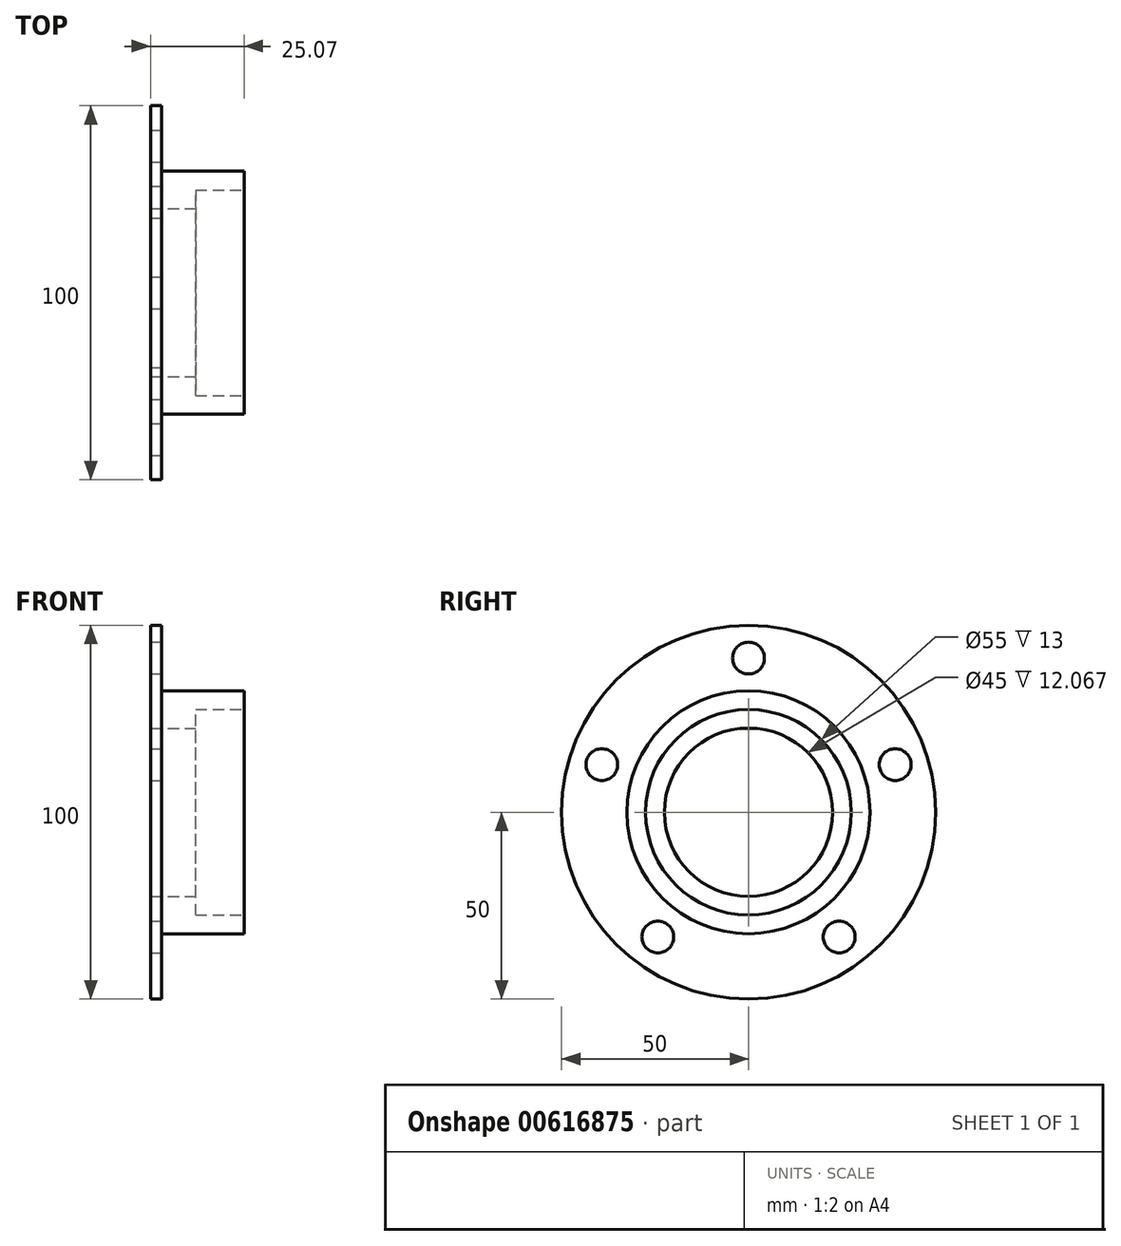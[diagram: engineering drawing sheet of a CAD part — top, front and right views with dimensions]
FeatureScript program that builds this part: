
annotation { "Feature Type Name" : "Feature", "Feature Type Description" : "" }
export const myFeature = defineFeature(function(context is Context, id is Id, definition is map)
    precondition{}
    {
        {
            var Q0;
            Q0=qCreatedBy(makeId("Front.planeOp"),FACE);
            var sketch = newSketch(context, id + "F0", { "sketchPlane" : qUnion([Q0])});
            skLineSegment(sketch, "E0", {"start": v(-2.43, 27.5) * mm, "end": v(-15.43, 27.5) * mm});
            skLineSegment(sketch, "E1", {"start": v(-15.43, 27.5) * mm, "end": v(-15.43, 22.5) * mm});
            skLineSegment(sketch, "E2", {"start": v(-15.43, 22.5) * mm, "end": v(-27.5, 22.5) * mm});
            skLineSegment(sketch, "E3", {"start": v(0, 0) * mm, "end": v(-125.94, 0) * mm, "construction": true});
            skLineSegment(sketch, "E4", {"start": v(-27.5, 22.5) * mm, "end": v(-27.5, 50) * mm});
            skLineSegment(sketch, "E5", {"start": v(-27.5, 50) * mm, "end": v(-24.5, 50) * mm});
            skLineSegment(sketch, "E6", {"start": v(-24.5, 50) * mm, "end": v(-24.5, 32.5) * mm});
            skLineSegment(sketch, "E7", {"start": v(-24.5, 32.5) * mm, "end": v(-2.43, 32.5) * mm});
            skLineSegment(sketch, "E8", {"start": v(-2.43, 32.5) * mm, "end": v(-2.43, 27.5) * mm});
            skSolve(sketch);
        }
        {
            var Q0;
            Q0=makeQuery(id+"F0.imprint","IMPRINT",FACE,{"disambiguationData":[TD([[makeQuery(id+"F0.imprint","IMPRINT",EDGE,{"derivedFrom":sQuery(id+"F0.wireOp",EDGE,"E0")}),-1.0]])]});
            var Q1;
            Q1=sQuery(id+"F0.wireOp",EDGE,"E3");
            revolve(context, id + "F1", {"surfaceOperationType" : NewSurfaceOperationType.NEW, "entities" : qUnion([Q0]), "axis" : qUnion([Q1]), "revolveType" : RevolveType.FULL});
        }
        {
            var Q0;
            Q0=makeQuery(id+"F1.opRevolve","SWEPT_FACE",FACE,{"disambiguationData":[OSD([sQuery(id+"F0.wireOp",EDGE,"E4")])]});
            var sketch = newSketch(context, id + "F2", { "sketchPlane" : qUnion([Q0])});
            skCircle(sketch, "E9", {"center": v(0, 0) * mm, "radius": 41.25 * mm, "construction": true});
            skCircle(sketch, "E10", {"center": v(0, 41.25) * mm, "radius": 5 * mm, "construction": true});
            skCircle(sketch, "E11.1.0", {"center": v(-39.23, 12.75) * mm, "radius": 5 * mm, "construction": true});
            skCircle(sketch, "E11.2.0", {"center": v(-24.25, -33.37) * mm, "radius": 5 * mm, "construction": true});
            skCircle(sketch, "E11.3.0", {"center": v(24.25, -33.37) * mm, "radius": 5 * mm, "construction": true});
            skCircle(sketch, "E11.4.0", {"center": v(39.23, 12.75) * mm, "radius": 5 * mm, "construction": true});
            skSolve(sketch);
        }
        {
            var Q0;
            Q0=sQuery(id+"F2.wireOp",VERTEX,"E10.center");
            var Q1;
            Q1=sQuery(id+"F2.wireOp",VERTEX,"E11.7.0.center");
            var Q2;
            Q2=sQuery(id+"F2.wireOp",VERTEX,"E11.6.0.center");
            var Q3;
            Q3=sQuery(id+"F2.wireOp",VERTEX,"E11.5.0.center");
            var Q4;
            Q4=sQuery(id+"F2.wireOp",VERTEX,"E11.4.0.center");
            var Q5;
            Q5=sQuery(id+"F2.wireOp",VERTEX,"E11.3.0.center");
            var Q6;
            Q6=sQuery(id+"F2.wireOp",VERTEX,"E11.2.0.center");
            var Q7;
            Q7=sQuery(id+"F2.wireOp",VERTEX,"E11.1.0.center");
            var Q8;
            Q8=makeQuery(id+"F1.opRevolve","SWEPT_BODY",BODY,{"disambiguationData":[OSD([sQuery(id+"F0.wireOp",EDGE,"7b1FusAU-kmKF-gHOi-H6g6-6aVmgGhASaw2"),sQuery(id+"F0.wireOp",EDGE,"E0"),sQuery(id+"F0.wireOp",EDGE,"LSGKa0bR-LwVC-EqDd-euec-UYEZ7jOWOLua"),sQuery(id+"F0.wireOp",EDGE,"5TDAa8MV-pvmY-Plpu-9oSZ-d0yG1KyHEeOB"),sQuery(id+"F0.wireOp",EDGE,"2wIOCRtX-0L1Q-h0eK-lsNd-ImzJ9RVkPgzw"),sQuery(id+"F0.wireOp",EDGE,"TBYgkJqi-TjOn-ymiA-IRIs-CuM3XwcQDRb2"),sQuery(id+"F0.wireOp",EDGE,"E1"),sQuery(id+"F0.wireOp",EDGE,"E2"),sQuery(id+"F0.wireOp",EDGE,"IG7HXhyX-9AKa-ksFD-AITW-nzrVQMC6C2Ye")])]});
            hole(context, id + "F3", {"style" : HoleStyle.SIMPLE, "endStyle" : HoleEndStyle.BLIND, "standardTappedOrClearance" : lookupTablePath({ "standard" : "ISO", "engagement" : "75%", "pitch" : "1.5 mm", "size" : "M10", "type" : "Tapped" }), "standardBlindInLast" : lookupTablePath({ "standard" : "ISO", "engagement" : "75%", "pitch" : "1.5 mm", "size" : "M10", "type" : "Tapped" }), "holeDiameter" : 8.5 * mm, "majorDiameter" : 10 * mm, "showTappedDepth" : true, "holeDepth" : 49.5 * mm, "isTappedThrough" : true, "tappedDepth" : 45 * mm, "tapClearance" : 3, "locations" : qUnion([Q0, Q1, Q2, Q3, Q4, Q5, Q6, Q7]), "scope" : qUnion([Q8]), "startStyle" : HoleStartStyle.PART});
        }
    });
